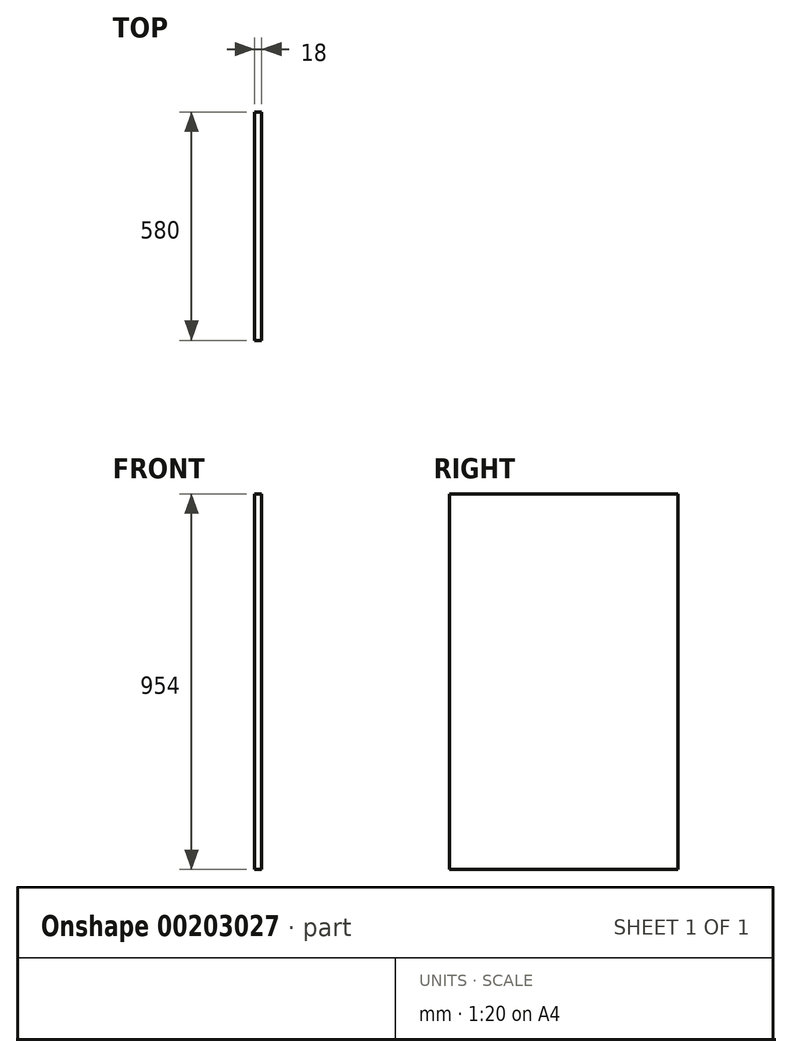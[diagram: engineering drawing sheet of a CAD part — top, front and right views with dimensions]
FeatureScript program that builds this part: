
annotation { "Feature Type Name" : "Feature", "Feature Type Description" : "" }
export const myFeature = defineFeature(function(context is Context, id is Id, definition is map)
    precondition{}
    {
        {
            var Q0;
            Q0=qCreatedBy(makeId("Right.planeOp"),FACE);
            var sketch = newSketch(context, id + "F0", { "sketchPlane" : qUnion([Q0])});
            skLineSegment(sketch, "E0.bottom", {"start": v(-290, -477) * mm, "end": v(290, -477) * mm});
            skLineSegment(sketch, "E0.top", {"start": v(-290, 477) * mm, "end": v(290, 477) * mm});
            skLineSegment(sketch, "E0.left", {"start": v(-290, -477) * mm, "end": v(-290, 477) * mm});
            skLineSegment(sketch, "E0.right", {"start": v(290, -477) * mm, "end": v(290, 477) * mm});
            skPoint(sketch, "E0.middle", {"position": v(0, 0) * mm});
            skSolve(sketch);
        }
        {
            var Q0;
            Q0 = qSketchRegion(id + "F0", true);
            extrude(context, id + "F1", {"entities" : qUnion([Q0]), "depth" : 18 * mm});
        }
    });
